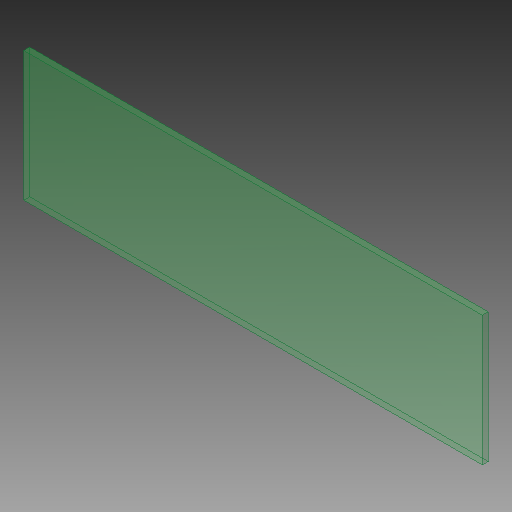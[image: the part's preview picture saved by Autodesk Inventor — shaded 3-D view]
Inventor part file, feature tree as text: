
AUTODESK INVENTOR PART (.ipt)
format: ipt  version: 2018.1 (Build 221171000, 171)  size: 101,376 bytes
history: native  units: mm
features: other x1, extrude x1, sketch x1
ambient origin geometry x8: Origin, YZ Plane, XZ Plane, XY Plane, X Axis, Y Axis, Z Axis, Center Point
bodies: Body1 (feature_tree)
feature tree (3):
  parser-record x1  (decoder bookkeeping rows leaked as tree rows — omitted from the tree; the rows remain in map.json)
  extrude  "Extrusion2"  Depth=110.0mm
  sketch  "Sketch2"  dims[d4=389.0mm d5=110.0mm d6=5.0mm d7=0.0mm]
note: 1 file-system path scrubbed to <path> (originals preserved in map.json)
